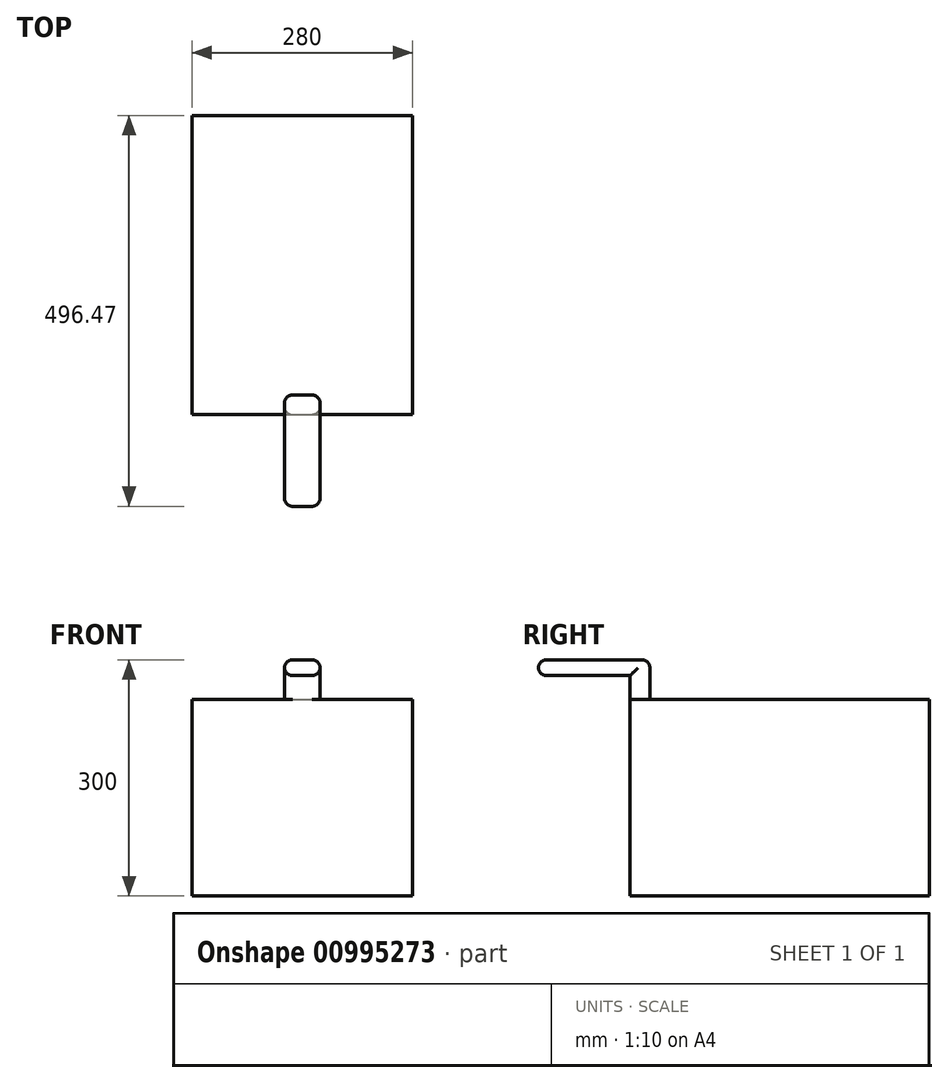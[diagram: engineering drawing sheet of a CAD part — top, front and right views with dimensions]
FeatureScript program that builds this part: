
annotation { "Feature Type Name" : "Feature", "Feature Type Description" : "" }
export const myFeature = defineFeature(function(context is Context, id is Id, definition is map)
    precondition{}
    {
        {
            var Q0;
            Q0=qCreatedBy(makeId("Top.planeOp"),FACE);
            var sketch = newSketch(context, id + "F0", { "sketchPlane" : qUnion([Q0])});
            skLineSegment(sketch, "E0.bottom", {"start": v(0, 0) * mm, "end": v(280, 0) * mm});
            skLineSegment(sketch, "E0.top", {"start": v(0, 380) * mm, "end": v(280, 380) * mm});
            skLineSegment(sketch, "E0.left", {"start": v(0, 0) * mm, "end": v(0, 380) * mm});
            skLineSegment(sketch, "E0.right", {"start": v(280, 0) * mm, "end": v(280, 380) * mm});
            skLineSegment(sketch, "E1", {"start": v(140, 0) * mm, "end": v(140, -116.47) * mm, "construction": true});
            skLineSegment(sketch, "E2", {"start": v(140, -116.47) * mm, "end": v(162.5, -116.47) * mm});
            skLineSegment(sketch, "E3", {"start": v(162.5, -116.47) * mm, "end": v(162.5, 0) * mm});
            skLineSegment(sketch, "E4.MirrorCS", {"start": v(117.5, -116.47) * mm, "end": v(117.5, 0) * mm});
            skLineSegment(sketch, "E5.MirrorCS", {"start": v(140, -116.47) * mm, "end": v(117.5, -116.47) * mm});
            skLineSegment(sketch, "E6", {"start": v(117.5, 0) * mm, "end": v(117.5, 25) * mm});
            skLineSegment(sketch, "E7", {"start": v(117.5, 25) * mm, "end": v(162.5, 25) * mm});
            skLineSegment(sketch, "E8", {"start": v(162.5, 0) * mm, "end": v(162.5, 25) * mm});
            skSolve(sketch);
        }
        {
            var Q0;
            Q0=makeQuery(id+"F0.imprint","IMPRINT",FACE,{"disambiguationData":[TD([[makeQuery(id+"F0.imprint","IMPRINT",EDGE,{"derivedFrom":sQuery(id+"F0.wireOp",EDGE,"E0.top")}),-1.0]])]});
            var Q1;
            {var subQ2=sQuery(id+"F0.wireOp",EDGE,"E6");Q1=makeQuery(id+"F0.imprint","IMPRINT",FACE,{"disambiguationData":[TD([[makeQuery(id+"F0.imprint","IMPRINT",EDGE,{"derivedFrom":subQ2}),-1.0]])]});}
            extrude(context, id + "F1", {"entities" : qUnion([Q0, Q1]), "depth" : 250 * mm, "offsetDistance" : 25 * mm});
        }
        {
            var Q0;
            {var subQ2=sQuery(id+"F0.wireOp",EDGE,"E6");Q0=makeQuery(id+"F0.imprint","IMPRINT",FACE,{"disambiguationData":[TD([[makeQuery(id+"F0.imprint","IMPRINT",EDGE,{"derivedFrom":subQ2}),-1.0]])]});}
            extrude(context, id + "F2", {"entities" : qUnion([Q0]), "operationType" : NewBodyOperationType.ADD, "depth" : 300 * mm, "offsetDistance" : 25 * mm, "hasSecondDirection" : true, "secondDirectionOppositeDirection" : false, "secondDirectionDepth" : 250 * mm});
        }
        {
            var Q0;
            Q0=makeQuery(id+"F0.imprint","IMPRINT",FACE,{"disambiguationData":[TD([[makeQuery(id+"F0.imprint","IMPRINT",EDGE,{"derivedFrom":sQuery(id+"F0.wireOp",EDGE,"E2")}),1.0]])]});
            extrude(context, id + "F3", {"entities" : qUnion([Q0]), "operationType" : NewBodyOperationType.ADD, "depth" : 300 * mm, "offsetDistance" : 25 * mm, "hasSecondDirection" : true, "secondDirectionOppositeDirection" : false, "secondDirectionDepth" : 280 * mm});
        }
        {
            var Q0;
            Q0=makeQuery(id+"F2.opExtrude","CAP_EDGE",EDGE,{"disambiguationData":[OSD([sQuery(id+"F0.wireOp",EDGE,"E7")])],"isStart":false});
            var Q1;
            Q1=makeQuery(id+"F3.boolean.opBoolean","MERGE",EDGE,{"derivedFrom":[makeQuery(id+"F2.opExtrude","CAP_EDGE",EDGE,{"disambiguationData":[OSD([sQuery(id+"F0.wireOp",EDGE,"E6")])],"isStart":false}),makeQuery(id+"F3.opExtrude","CAP_EDGE",EDGE,{"disambiguationData":[OSD([sQuery(id+"F0.wireOp",EDGE,"E4.MirrorCS")])],"isStart":false})]});
            var Q2;
            Q2=makeQuery(id+"F3.boolean.opBoolean","MERGE",EDGE,{"derivedFrom":[makeQuery(id+"F2.opExtrude","CAP_EDGE",EDGE,{"disambiguationData":[OSD([sQuery(id+"F0.wireOp",EDGE,"E8")])],"isStart":false}),makeQuery(id+"F3.opExtrude","CAP_EDGE",EDGE,{"disambiguationData":[OSD([sQuery(id+"F0.wireOp",EDGE,"E3")])],"isStart":false})]});
            var Q3;
            Q3=makeQuery(id+"F2.opExtrude","SWEPT_EDGE",EDGE,{"disambiguationData":[OSD([sQuery(id+"F0.wireOp",EDGE,"E7"),sQuery(id+"F0.wireOp",EDGE,"E8")])]});
            var Q4;
            Q4=makeQuery(id+"F2.opExtrude","SWEPT_EDGE",EDGE,{"disambiguationData":[OSD([sQuery(id+"F0.wireOp",EDGE,"E6"),sQuery(id+"F0.wireOp",EDGE,"E7")])]});
            var Q5;
            Q5=makeQuery(id+"F3.opExtrude","CAP_EDGE",EDGE,{"disambiguationData":[OSD([sQuery(id+"F0.wireOp",EDGE,"E3")])],"isStart":true});
            var Q6;
            Q6=makeQuery(id+"F3.opExtrude","CAP_EDGE",EDGE,{"disambiguationData":[OSD([sQuery(id+"F0.wireOp",EDGE,"E4.MirrorCS")])],"isStart":true});
            var Q7;
            Q7=makeQuery(id+"F2.opExtrude","SWEPT_EDGE",EDGE,{"disambiguationData":[OSD([sQuery(id+"F0.wireOp",EDGE,"E0.bottom"),sQuery(id+"F0.wireOp",EDGE,"E3"),sQuery(id+"F0.wireOp",EDGE,"E8")])]});
            var Q8;
            Q8=makeQuery(id+"F2.opExtrude","SWEPT_EDGE",EDGE,{"disambiguationData":[OSD([sQuery(id+"F0.wireOp",EDGE,"E0.bottom"),sQuery(id+"F0.wireOp",EDGE,"E4.MirrorCS"),sQuery(id+"F0.wireOp",EDGE,"E6")])]});
            var Q9;
            Q9=makeQuery(id+"F3.opExtrude","SWEPT_FACE",FACE,{"disambiguationData":[OSD([sQuery(id+"F0.wireOp",EDGE,"E2"),sQuery(id+"F0.wireOp",EDGE,"E5.MirrorCS")])]});
            fillet(context, id + "F4", {"entities" : qUnion([Q0, Q1, Q2, Q3, Q4, Q5, Q6, Q7, Q8, Q9]), "radius" : 10 * mm, "tangentPropagation" : true, "allowEdgeOverflow" : false});
        }
    });
